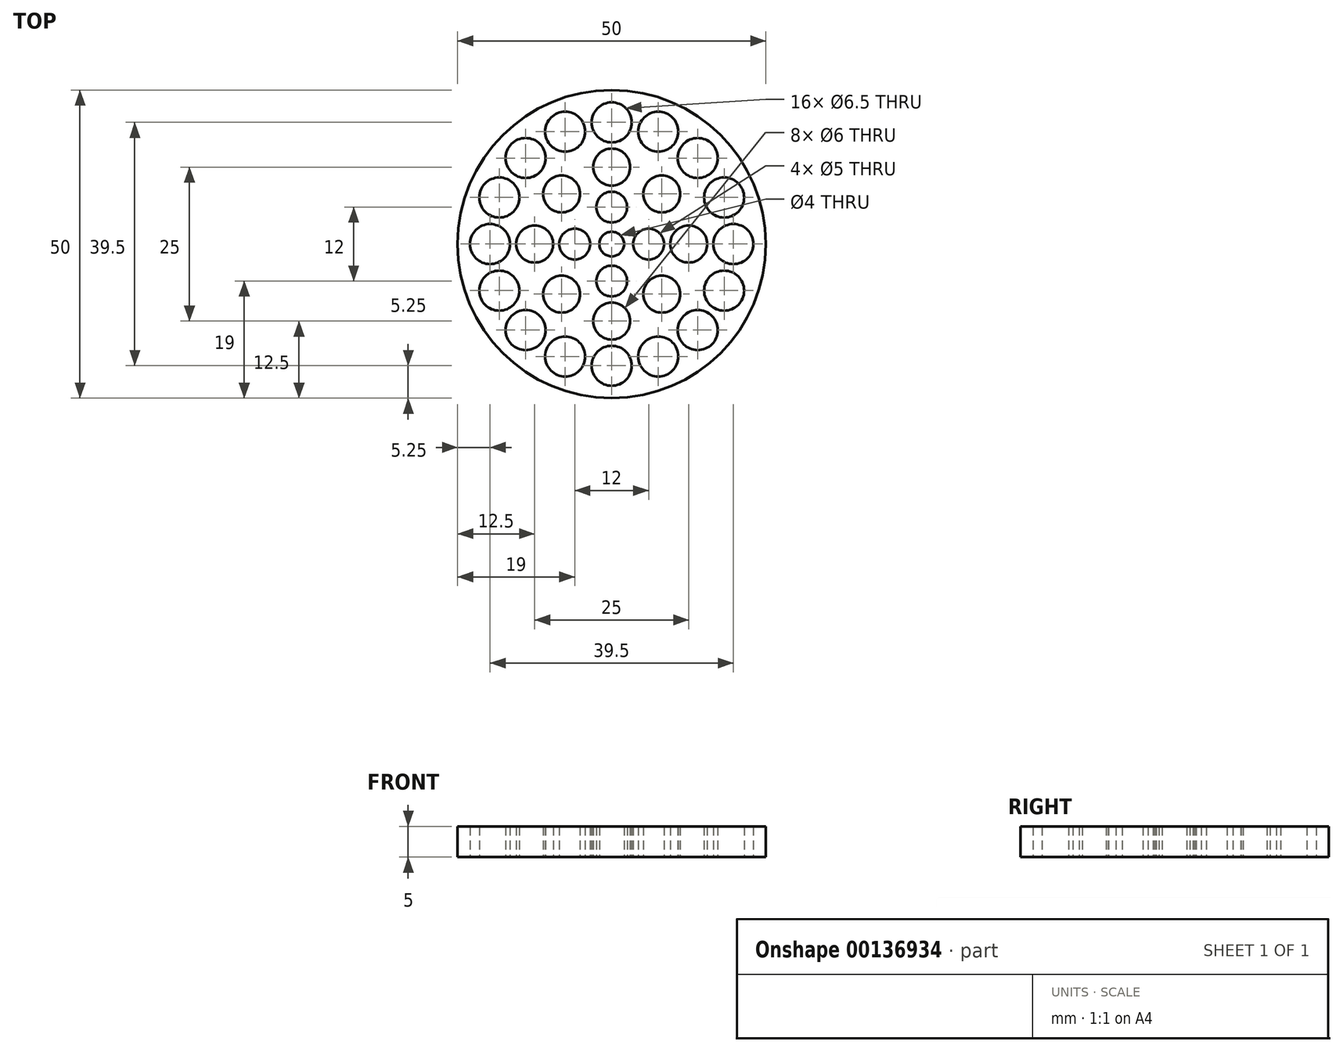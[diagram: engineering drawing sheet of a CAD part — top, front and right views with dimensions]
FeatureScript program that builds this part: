
annotation { "Feature Type Name" : "Feature", "Feature Type Description" : "" }
export const myFeature = defineFeature(function(context is Context, id is Id, definition is map)
    precondition{}
    {
        {
            var Q0;
            Q0=qCreatedBy(makeId("Top.planeOp"),FACE);
            var sketch = newSketch(context, id + "F0", { "sketchPlane" : qUnion([Q0])});
            skCircle(sketch, "E0", {"center": v(0, 0) * mm, "radius": 25 * mm});
            skCircle(sketch, "E1", {"center": v(0, 19.75) * mm, "radius": 3.25 * mm});
            skCircle(sketch, "E2", {"center": v(0, 12.5) * mm, "radius": 3 * mm});
            skCircle(sketch, "E3", {"center": v(0, 6) * mm, "radius": 2.5 * mm});
            skCircle(sketch, "E4", {"center": v(0, 0) * mm, "radius": 2 * mm});
            skCircle(sketch, "E5", {"center": v(6, 0) * mm, "radius": 2.5 * mm});
            skCircle(sketch, "E6", {"center": v(12.5, 0) * mm, "radius": 3 * mm});
            skCircle(sketch, "E7", {"center": v(19.75, 0) * mm, "radius": 3.25 * mm});
            skCircle(sketch, "E8", {"center": v(0, -6) * mm, "radius": 2.5 * mm});
            skCircle(sketch, "E9", {"center": v(0, -12.5) * mm, "radius": 3 * mm});
            skCircle(sketch, "E10", {"center": v(0, -19.75) * mm, "radius": 3.25 * mm});
            skCircle(sketch, "E11", {"center": v(-6, 0) * mm, "radius": 2.5 * mm});
            skCircle(sketch, "E12", {"center": v(-12.5, 0) * mm, "radius": 3 * mm});
            skCircle(sketch, "E13", {"center": v(-19.75, 0) * mm, "radius": 3.25 * mm});
            skCircle(sketch, "E14", {"center": v(13.97, 13.97) * mm, "radius": 3.25 * mm});
            skCircle(sketch, "E15", {"center": v(-13.97, 13.97) * mm, "radius": 3.25 * mm});
            skCircle(sketch, "E16", {"center": v(-13.97, -13.97) * mm, "radius": 3.25 * mm});
            skCircle(sketch, "E17", {"center": v(13.97, -13.97) * mm, "radius": 3.25 * mm});
            skCircle(sketch, "E18", {"center": v(8.13, -8.13) * mm, "radius": 3 * mm});
            skCircle(sketch, "E19", {"center": v(8.13, 8.13) * mm, "radius": 3 * mm});
            skCircle(sketch, "E20", {"center": v(-8.13, 8.13) * mm, "radius": 3 * mm});
            skCircle(sketch, "E21", {"center": v(-8.13, -8.13) * mm, "radius": 3 * mm});
            skCircle(sketch, "E22", {"center": v(-18.25, 7.56) * mm, "radius": 3.25 * mm});
            skCircle(sketch, "E23", {"center": v(-7.56, 18.25) * mm, "radius": 3.25 * mm});
            skCircle(sketch, "E24", {"center": v(7.56, 18.25) * mm, "radius": 3.25 * mm});
            skCircle(sketch, "E25", {"center": v(-18.25, -7.56) * mm, "radius": 3.25 * mm});
            skCircle(sketch, "E26", {"center": v(7.56, -18.25) * mm, "radius": 3.25 * mm});
            skCircle(sketch, "E27", {"center": v(-7.56, -18.25) * mm, "radius": 3.25 * mm});
            skCircle(sketch, "E28", {"center": v(18.25, -7.56) * mm, "radius": 3.25 * mm});
            skCircle(sketch, "E29", {"center": v(18.25, 7.56) * mm, "radius": 3.25 * mm});
            skSolve(sketch);
        }
        {
            var Q0;
            Q0=makeQuery(id+"F0.imprint","IMPRINT",FACE,{"disambiguationData":[TD([[makeQuery(id+"F0.imprint","IMPRINT",EDGE,{"derivedFrom":sQuery(id+"F0.wireOp",EDGE,"E0")}),1.0]])]});
            extrude(context, id + "F1", {"entities" : qUnion([Q0]), "depth" : 5 * mm});
        }
    });
